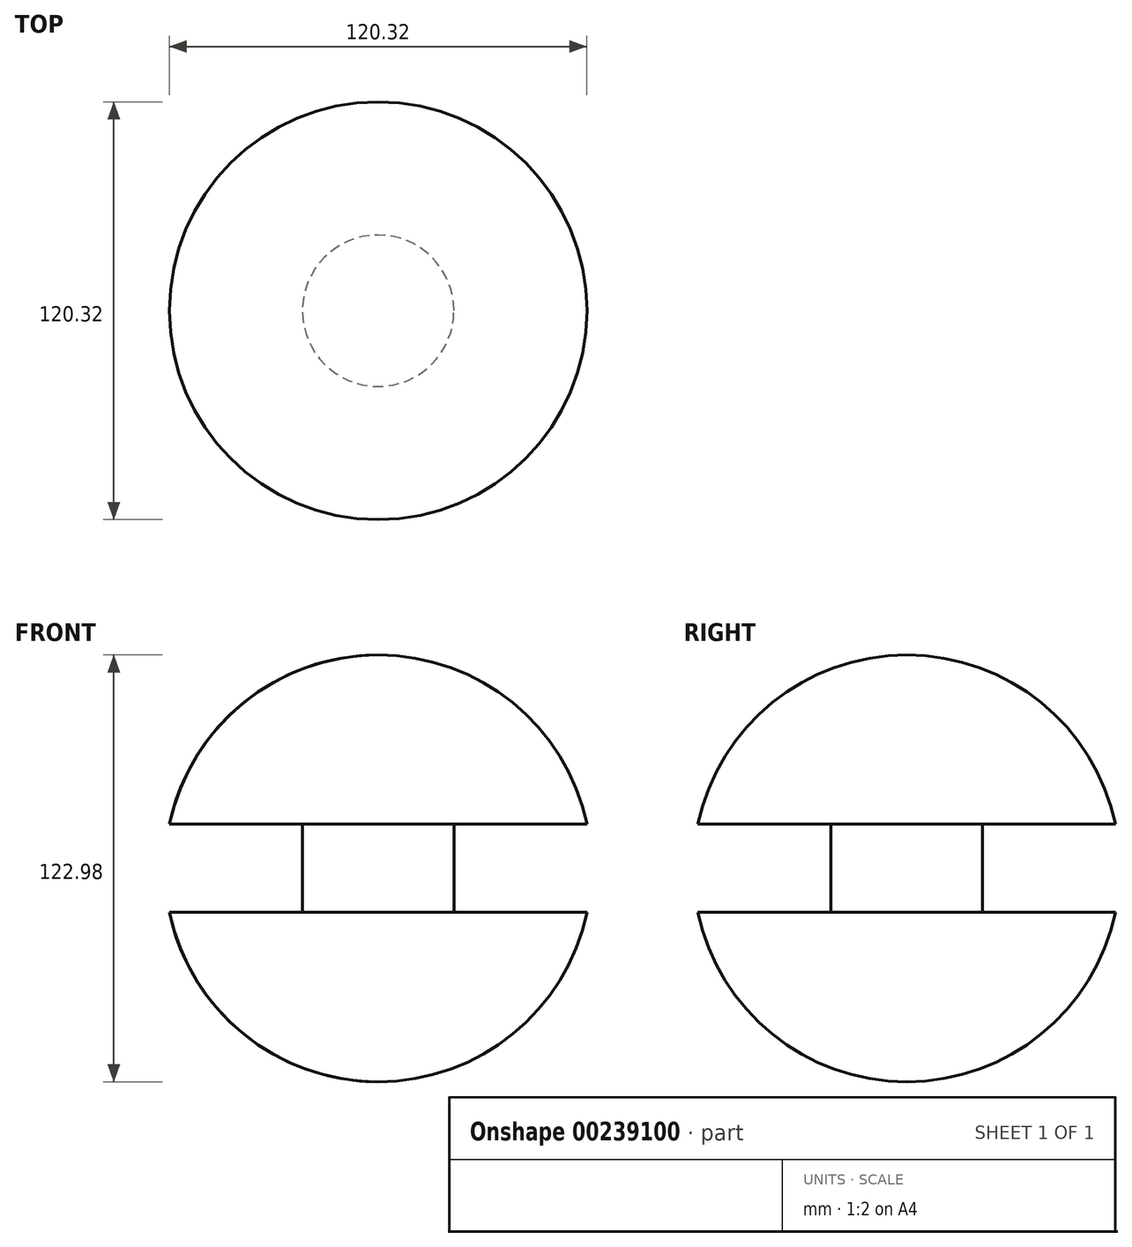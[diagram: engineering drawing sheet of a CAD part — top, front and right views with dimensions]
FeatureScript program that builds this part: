
annotation { "Feature Type Name" : "Feature", "Feature Type Description" : "" }
export const myFeature = defineFeature(function(context is Context, id is Id, definition is map)
    precondition{}
    {
        {
            var Q0;
            Q0=qCreatedBy(makeId("Front.planeOp"),FACE);
            var sketch = newSketch(context, id + "F0", { "sketchPlane" : qUnion([Q0])});
            skArc(sketch, "E0", {"start": v(0, -61.49) * mm, "mid": v(61.49, 0) * mm, "end": v(0, 61.49) * mm});
            skLineSegment(sketch, "E1", {"start": v(0, 61.49) * mm, "end": v(0, -61.49) * mm});
            skSolve(sketch);
        }
        {
            var Q0;
            Q0 = qSketchRegion(id + "F0", true);
            var Q1;
            Q1=sQuery(id+"F0.wireOp",EDGE,"E1");
            revolve(context, id + "F1", {"entities" : qUnion([Q0]), "axis" : qUnion([Q1]), "revolveType" : RevolveType.FULL});
        }
        {
            var Q0;
            Q0=qCreatedBy(makeId("Front.planeOp"),FACE);
            var sketch = newSketch(context, id + "F2", { "sketchPlane" : qUnion([Q0])});
            skLineSegment(sketch, "E2", {"start": v(0, 47.21) * mm, "end": v(0, -52.73) * mm, "construction": true});
            skLineSegment(sketch, "E3.bottom", {"start": v(21.81, 12.7) * mm, "end": v(77.58, 12.7) * mm});
            skLineSegment(sketch, "E3.top", {"start": v(21.81, -12.7) * mm, "end": v(77.58, -12.7) * mm});
            skLineSegment(sketch, "E3.left", {"start": v(21.81, 12.7) * mm, "end": v(21.81, -12.7) * mm});
            skLineSegment(sketch, "E3.right", {"start": v(77.58, 12.7) * mm, "end": v(77.58, -12.7) * mm});
            skPoint(sketch, "E3.middle", {"position": v(49.7, 0) * mm});
            skSolve(sketch);
        }
        {
            var Q0;
            Q0 = qSketchRegion(id + "F2", true);
            var Q1;
            Q1=sQuery(id+"F2.wireOp",EDGE,"E2");
            revolve(context, id + "F3", {"operationType" : NewBodyOperationType.REMOVE, "entities" : qUnion([Q0]), "axis" : qUnion([Q1]), "revolveType" : RevolveType.FULL, "oppositeDirection" : true});
        }
    });
